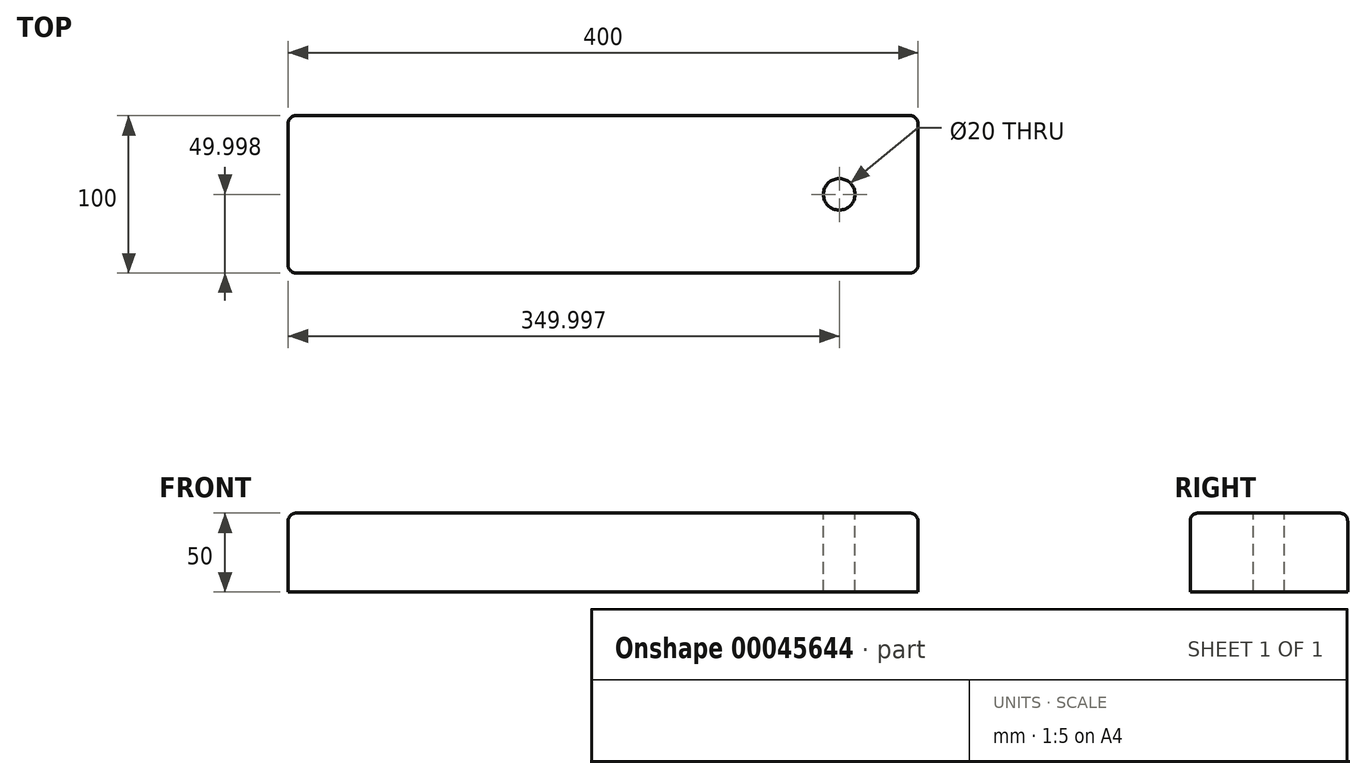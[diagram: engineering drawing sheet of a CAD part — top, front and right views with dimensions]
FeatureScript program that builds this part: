
annotation { "Feature Type Name" : "Feature", "Feature Type Description" : "" }
export const myFeature = defineFeature(function(context is Context, id is Id, definition is map)
    precondition{}
    {
        {
            var Q0;
            Q0=qCreatedBy(makeId("Top.planeOp"),FACE);
            var sketch = newSketch(context, id + "F0", { "sketchPlane" : qUnion([Q0])});
            skLineSegment(sketch, "E0.bottom", {"start": v(-200.92, -34.6) * mm, "end": v(199.08, -34.6) * mm});
            skLineSegment(sketch, "E0.top", {"start": v(-200.92, 65.4) * mm, "end": v(199.08, 65.4) * mm});
            skLineSegment(sketch, "E0.left", {"start": v(-200.92, -34.6) * mm, "end": v(-200.92, 65.4) * mm});
            skLineSegment(sketch, "E0.right", {"start": v(199.08, -34.6) * mm, "end": v(199.08, 65.4) * mm});
            skSolve(sketch);
        }
        {
            var Q0;
            Q0=makeQuery(id+"F0.imprint","IMPRINT",FACE,{"disambiguationData":[TD([[makeQuery(id+"F0.imprint","IMPRINT",EDGE,{"derivedFrom":sQuery(id+"F0.wireOp",EDGE,"E0.bottom")}),1.0]])]});
            extrude(context, id + "F1", {"entities" : qUnion([Q0]), "depth" : 50 * mm});
        }
        {
            var Q0;
            Q0=makeQuery(id+"F1.opExtrude","SWEPT_EDGE",EDGE,{"disambiguationData":[OSD([sQuery(id+"F0.wireOp",EDGE,"E0.bottom"),sQuery(id+"F0.wireOp",EDGE,"E0.left")])]});
            var Q1;
            Q1=makeQuery(id+"F1.opExtrude","SWEPT_EDGE",EDGE,{"disambiguationData":[OSD([sQuery(id+"F0.wireOp",EDGE,"E0.bottom"),sQuery(id+"F0.wireOp",EDGE,"E0.right")])]});
            var Q2;
            Q2=makeQuery(id+"F1.opExtrude","SWEPT_EDGE",EDGE,{"disambiguationData":[OSD([sQuery(id+"F0.wireOp",EDGE,"E0.top"),sQuery(id+"F0.wireOp",EDGE,"E0.right")])]});
            var Q3;
            Q3=makeQuery(id+"F1.opExtrude","CAP_EDGE",EDGE,{"disambiguationData":[OSD([sQuery(id+"F0.wireOp",EDGE,"E0.right")])],"isStart":false});
            var Q4;
            Q4=makeQuery(id+"F1.opExtrude","CAP_EDGE",EDGE,{"disambiguationData":[OSD([sQuery(id+"F0.wireOp",EDGE,"E0.bottom")])],"isStart":false});
            var Q5;
            Q5=makeQuery(id+"F1.opExtrude","CAP_EDGE",EDGE,{"disambiguationData":[OSD([sQuery(id+"F0.wireOp",EDGE,"E0.top")])],"isStart":false});
            fillet(context, id + "F2", {"entities" : qUnion([Q0, Q1, Q2, Q3, Q4, Q5]), "radius" : 5 * mm, "tangentPropagation" : true, "allowEdgeOverflow" : false});
        }
        {
            var Q0;
            Q0=makeQuery(id+"F1.opExtrude","SWEPT_EDGE",EDGE,{"disambiguationData":[OSD([sQuery(id+"F0.wireOp",EDGE,"E0.top"),sQuery(id+"F0.wireOp",EDGE,"E0.left")])]});
            fillet(context, id + "F3", {"entities" : qUnion([Q0]), "radius" : 5 * mm, "tangentPropagation" : true, "allowEdgeOverflow" : false});
        }
        {
            var Q0;
            Q0=makeQuery(id+"F1.opExtrude","CAP_FACE",FACE,{"disambiguationData":[OSD([sQuery(id+"F0.wireOp",EDGE,"E0.bottom"),sQuery(id+"F0.wireOp",EDGE,"E0.top"),sQuery(id+"F0.wireOp",EDGE,"E0.left"),sQuery(id+"F0.wireOp",EDGE,"E0.right")])],"isStart":false});
            var sketch = newSketch(context, id + "F4", { "sketchPlane" : qUnion([Q0])});
            skCircle(sketch, "E1", {"center": v(149.08, 15.4) * mm, "radius": 10 * mm});
            skSolve(sketch);
        }
        {
            var Q0;
            Q0 = qSketchRegion(id + "F4", true);
            extrude(context, id + "F5", {"entities" : qUnion([Q0]), "operationType" : NewBodyOperationType.REMOVE, "endBound" : BoundingType.THROUGH_ALL, "oppositeDirection" : true, "depth" : 25 * mm});
        }
    });
